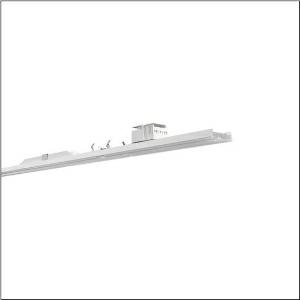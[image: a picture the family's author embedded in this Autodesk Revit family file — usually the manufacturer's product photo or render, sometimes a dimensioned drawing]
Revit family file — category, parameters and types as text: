
# Revit family: licross_r__11_recessed_mo_51tl11cn48xfd_8f5b
name_source: partatom
category: Lighting Fixtures
units: mm (PartAtom-declared; Revit-internal decimal feet)

## family parameters
Cut with Voids When Loaded = No
Host = Face
Light Source = No
Part Type = Normal
Room Calculation Point = No
Round Connector Dimension = Use Diameter
Shared = No

## types (1)
- --- (1 x LED, 3370 lm, 22.1 W, 4000K)
    Apparent Load = 22 VA
    CIE Flux Codes = 89 96 99 100 100
    Color Rendering = 80
    Color Temperature = 4000K
    Default Elevation = 1800 mm
    Description = Licross® 11 Recessed MOluminaire insert, length: 1.500mm, width: 66mm, height: 67mm, LED rated luminous flux: 8.170lm, light colour: 840, control gear: ON/OFF Multilumen, CLOi, control gear: ECG Multilumen, with plug, 6-pole, with phase selection, mains connection: 220..240V, AC/DC, 0/50..60Hz, without changeover relay, for emergency light function, for central battery installations according to DIN EN 60598-2-22, halogen-free wiring, primary optical cover: cover, of PMMA, light emission: direct distribution, protection rating (complete): IP40, insulation class (complete): insulation class I (protective earthing), certification: CE, ENEC, VDE, protection symbol: D if used in an environment without relevant dust loads with corresponding accessories, permissible ambient temperature for indoor applications: -35..+40°C, standard: EN 60598-2-22, reducing of maximum allowable ambient temperature of 5°C with ceiling mounting, corresponds to IFS (International Featured Standards) requirements for safety and quality in the food industry, packaging unit: 1 piece
    Height = 58 mm
    Lamp = 1 x LED
    Lamp Light Flux = 3370 lm
    Lamp Power = 22.1 W
    Lamp count = 1
    Length = 1500 mm
    Luminous efficacy = 152 lm/W
    Manufacturer = Siteco
    ModVariant = No
    Model = 51TL11CN48XFD
    Mounting Place = Ceiling
    Mounting Type = Pendant
    Number of Poles = 1
    OnlyDefault = Yes
    Power Factor = 1
    Product Name = Licross® 11 Recessed MO
    Product group = luminaire insert
    ProductGroupID = 902
    Protection Class = Protection class I
    Protection Degree = IP 40
    RLX_Detail_Level = 1
    RlxData = <blob elided: 20465 chars, md5=28e88c23>
    Socket = socket
    Standby Power = 0 W
    System Light Flux = 3370 lm
    System Power = 22 W
    Type Comments = : DC mode (central or group accumulator) initial emergency light level
    Type Image = l_1266722.jpg
    URL = http://relux.com
    VarID = @adj_134047
    Voltage = 0 V
    Weight = 0.00 kg
    Width = 66 mm

## geometry (parser evidence)
native form markers: Blend x4, Sweep x12
no freeform markers — native parametric forms only
